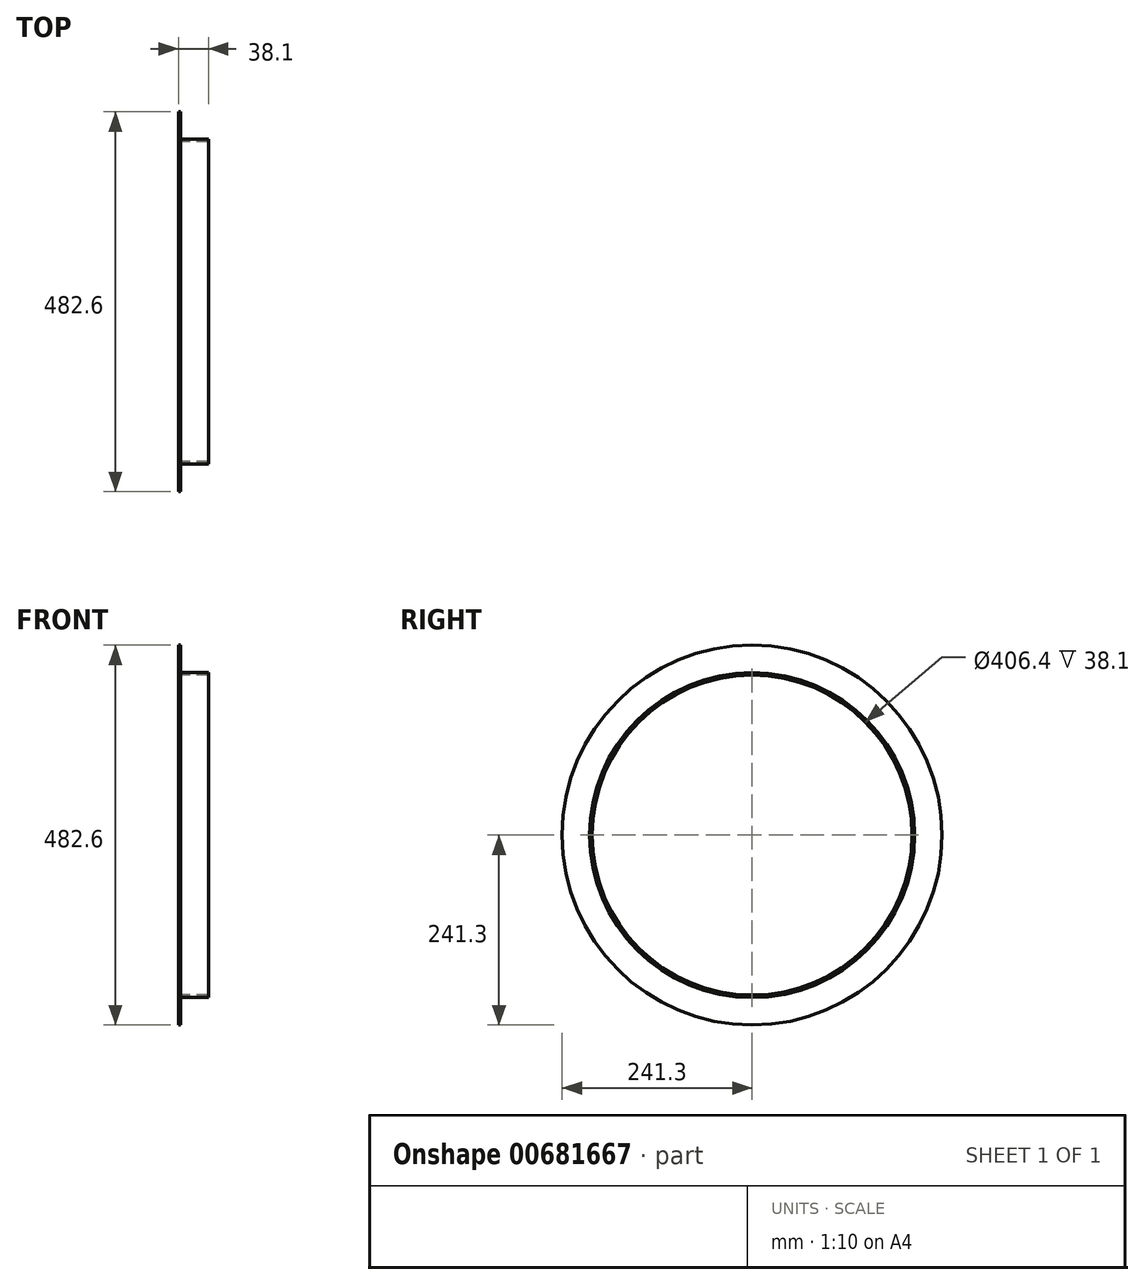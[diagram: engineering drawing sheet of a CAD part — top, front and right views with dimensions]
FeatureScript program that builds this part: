
annotation { "Feature Type Name" : "Feature", "Feature Type Description" : "" }
export const myFeature = defineFeature(function(context is Context, id is Id, definition is map)
    precondition{}
    {
        {
            var Q0;
            Q0=qCreatedBy(makeId("Front.planeOp"),FACE);
            var sketch = newSketch(context, id + "F0", { "sketchPlane" : qUnion([Q0])});
            skLineSegment(sketch, "E0", {"start": v(0, 0) * mm, "end": v(0, 38.1) * mm});
            skLineSegment(sketch, "E1", {"start": v(0, 38.1) * mm, "end": v(3.17, 38.1) * mm});
            skLineSegment(sketch, "E2", {"start": v(3.17, 38.1) * mm, "end": v(3.17, 3.17) * mm});
            skLineSegment(sketch, "E3", {"start": v(3.18, 3.17) * mm, "end": v(38.1, 3.17) * mm});
            skLineSegment(sketch, "E4", {"start": v(38.1, 3.17) * mm, "end": v(38.1, 0) * mm});
            skLineSegment(sketch, "E5", {"start": v(38.1, 0) * mm, "end": v(0, 0) * mm});
            skLineSegment(sketch, "E6", {"start": v(0, 0) * mm, "end": v(0, -203.2) * mm});
            skLineSegment(sketch, "E7", {"start": v(0, -203.2) * mm, "end": v(66.55, -203.2) * mm});
            skSolve(sketch);
        }
        {
            var Q0;
            Q0=makeQuery(id+"F0.imprint","IMPRINT",FACE,{"disambiguationData":[TD([[makeQuery(id+"F0.imprint","IMPRINT",EDGE,{"derivedFrom":sQuery(id+"F0.wireOp",EDGE,"E0")}),-1.0]])]});
            var Q1;
            Q1=sQuery(id+"F0.wireOp",EDGE,"E7");
            revolve(context, id + "F1", {"surfaceOperationType" : NewSurfaceOperationType.NEW, "entities" : qUnion([Q0]), "axis" : qUnion([Q1]), "revolveType" : RevolveType.FULL});
        }
    });
